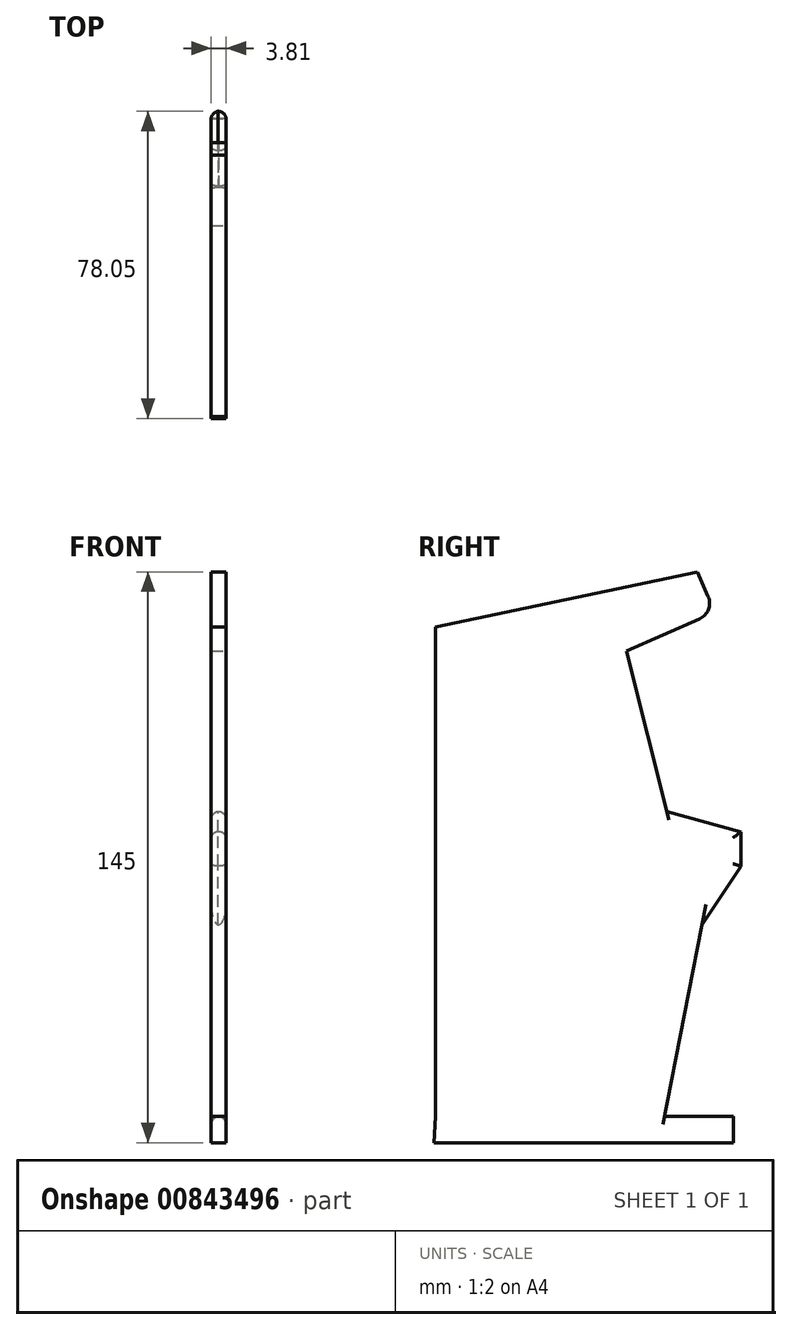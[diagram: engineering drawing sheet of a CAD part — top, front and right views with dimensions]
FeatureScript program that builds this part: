
annotation { "Feature Type Name" : "Feature", "Feature Type Description" : "" }
export const myFeature = defineFeature(function(context is Context, id is Id, definition is map)
    precondition{}
    {
        {
            var Q0;
            Q0=qCreatedBy(makeId("Right.planeOp"),FACE);
            var sketch = newSketch(context, id + "F0", { "sketchPlane" : qUnion([Q0])});
            skLineSegment(sketch, "E0", {"start": v(-45.1, 37.53) * mm, "end": v(-45.1, -59.92) * mm});
            skLineSegment(sketch, "E1", {"start": v(22.55, -11.2) * mm, "end": v(32.48, 3.7) * mm});
            skLineSegment(sketch, "E2", {"start": v(32.48, 3.7) * mm, "end": v(32.48, 12.46) * mm});
            skLineSegment(sketch, "E3", {"start": v(32.48, 12.46) * mm, "end": v(13.56, 17.66) * mm});
            skLineSegment(sketch, "E4", {"start": v(13.56, 17.66) * mm, "end": v(3.4, 58.34) * mm});
            skLineSegment(sketch, "E5", {"start": v(3.4, 58.34) * mm, "end": v(25.86, 68.28) * mm});
            skLineSegment(sketch, "E6", {"start": v(25.86, 68.28) * mm, "end": v(21.36, 78.46) * mm});
            skLineSegment(sketch, "E7", {"start": v(21.36, 78.46) * mm, "end": v(-45.1, 64.5) * mm});
            skLineSegment(sketch, "E8", {"start": v(-45.1, 64.5) * mm, "end": v(-45.1, 31.85) * mm});
            skLineSegment(sketch, "E9", {"start": v(-45.1, 31.85) * mm, "end": v(-45.1, -59.92) * mm});
            skLineSegment(sketch, "E10", {"start": v(22.55, -11.2) * mm, "end": v(13.09, -59.92) * mm});
            skLineSegment(sketch, "E11", {"start": v(13.09, -59.92) * mm, "end": v(30.6, -59.92) * mm});
            skLineSegment(sketch, "E12", {"start": v(30.6, -59.92) * mm, "end": v(30.6, -66.54) * mm});
            skLineSegment(sketch, "E13", {"start": v(30.6, -66.54) * mm, "end": v(-45.57, -66.54) * mm});
            skLineSegment(sketch, "E14", {"start": v(-45.57, -66.54) * mm, "end": v(-45.1, -59.92) * mm});
            skSolve(sketch);
        }
        {
            var Q0;
            Q0=makeQuery(id+"F0.imprint","IMPRINT",FACE,{"disambiguationData":[TD([[makeQuery(id+"F0.imprint","IMPRINT",EDGE,{"derivedFrom":sQuery(id+"F0.wireOp",EDGE,"E1")}),1.0]])]});
            extrude(context, id + "F1", {"entities" : qUnion([Q0]), "oppositeDirection" : true, "depth" : 3.8 * mm, "offsetDistance" : 25.4 * mm});
        }
        {
            var Q0;
            Q0=makeQuery(id+"F1.opExtrude","CAP_EDGE",EDGE,{"disambiguationData":[OSD([sQuery(id+"F0.wireOp",EDGE,"E3")])],"isStart":true});
            var Q1;
            Q1=makeQuery(id+"F1.opExtrude","CAP_EDGE",EDGE,{"disambiguationData":[OSD([sQuery(id+"F0.wireOp",EDGE,"E1")])],"isStart":true});
            var Q2;
            Q2=makeQuery(id+"F1.opExtrude","CAP_EDGE",EDGE,{"disambiguationData":[OSD([sQuery(id+"F0.wireOp",EDGE,"E2")])],"isStart":true});
            fillet(context, id + "F2", {"entities" : qUnion([Q0, Q1, Q2]), "radius" : 2.03 * mm, "tangentPropagation" : true, "allowEdgeOverflow" : false});
        }
        {
            var Q0;
            Q0=makeQuery(id+"F1.opExtrude","CAP_EDGE",EDGE,{"disambiguationData":[OSD([sQuery(id+"F0.wireOp",EDGE,"E3")])],"isStart":false});
            var Q1;
            Q1=makeQuery(id+"F1.opExtrude","CAP_EDGE",EDGE,{"disambiguationData":[OSD([sQuery(id+"F0.wireOp",EDGE,"E1")])],"isStart":false});
            var Q2;
            Q2=makeQuery(id+"F1.opExtrude","CAP_EDGE",EDGE,{"disambiguationData":[OSD([sQuery(id+"F0.wireOp",EDGE,"E2")])],"isStart":false});
            fillet(context, id + "F3", {"entities" : qUnion([Q0, Q1, Q2]), "radius" : 2.03 * mm, "tangentPropagation" : true, "allowEdgeOverflow" : false});
        }
        {
            var Q0;
            Q0=makeQuery(id+"F1.opExtrude","SWEPT_EDGE",EDGE,{"disambiguationData":[OSD([sQuery(id+"F0.wireOp",EDGE,"E5"),sQuery(id+"F0.wireOp",EDGE,"E6")])]});
            fillet(context, id + "F4", {"entities" : qUnion([Q0]), "radius" : 4.3 * mm, "tangentPropagation" : true, "allowEdgeOverflow" : false});
        }
        {
            var Q0;
            Q0=makeQuery(id+"F1.opExtrude","CAP_EDGE",EDGE,{"disambiguationData":[OSD([sQuery(id+"F0.wireOp",EDGE,"E11")])],"isStart":false});
            fillet(context, id + "F5", {"entities" : qUnion([Q0]), "radius" : 2.03 * mm, "tangentPropagation" : true, "allowEdgeOverflow" : false});
        }
        {
            var Q0;
            Q0=makeQuery(id+"F1.opExtrude","CAP_EDGE",EDGE,{"disambiguationData":[OSD([sQuery(id+"F0.wireOp",EDGE,"E11")])],"isStart":true});
            fillet(context, id + "F6", {"entities" : qUnion([Q0]), "radius" : 2.03 * mm, "tangentPropagation" : true, "allowEdgeOverflow" : false});
        }
    });
